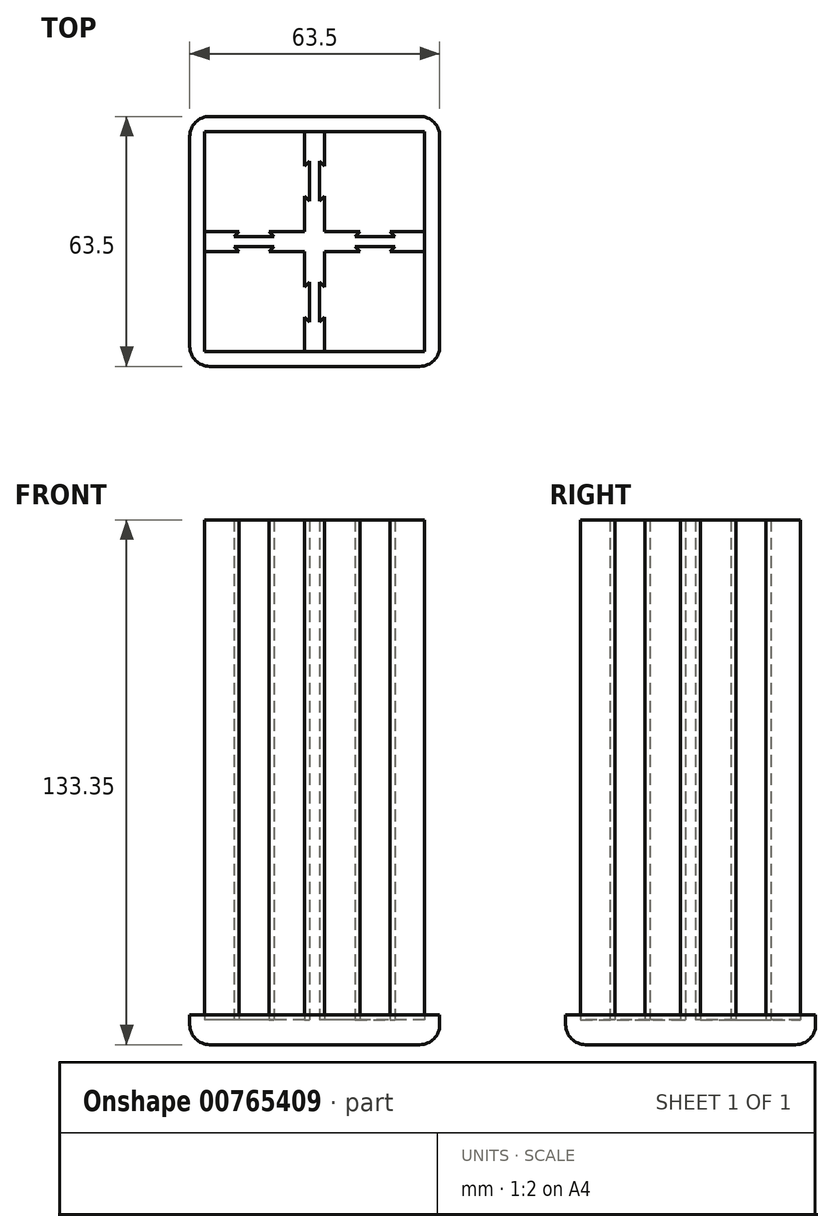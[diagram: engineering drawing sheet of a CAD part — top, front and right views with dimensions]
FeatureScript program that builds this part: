
annotation { "Feature Type Name" : "Feature", "Feature Type Description" : "" }
export const myFeature = defineFeature(function(context is Context, id is Id, definition is map)
    precondition{}
    {
        {
            var Q0;
            Q0=qCreatedBy(makeId("Top.planeOp"),FACE);
            var sketch = newSketch(context, id + "F0", { "sketchPlane" : qUnion([Q0])});
            skLineSegment(sketch, "E0.bottom", {"start": v(-2.54, 27.94) * mm, "end": v(2.54, 27.94) * mm});
            skLineSegment(sketch, "E0.top", {"start": v(-2.54, -27.94) * mm, "end": v(2.54, -27.94) * mm});
            skLineSegment(sketch, "E0.left", {"start": v(-2.54, 27.94) * mm, "end": v(-2.54, -27.94) * mm});
            skLineSegment(sketch, "E0.right", {"start": v(2.54, 27.94) * mm, "end": v(2.54, -27.94) * mm});
            skPoint(sketch, "E0.middle", {"position": v(0, 0) * mm});
            skLineSegment(sketch, "E1.bottom", {"start": v(27.94, 2.54) * mm, "end": v(-27.94, 2.54) * mm});
            skLineSegment(sketch, "E1.top", {"start": v(27.94, -2.54) * mm, "end": v(-27.94, -2.54) * mm});
            skLineSegment(sketch, "E1.left", {"start": v(27.94, 2.54) * mm, "end": v(27.94, -2.54) * mm});
            skLineSegment(sketch, "E1.right", {"start": v(-27.94, 2.54) * mm, "end": v(-27.94, -2.54) * mm});
            skLineSegment(sketch, "E2.bottom", {"start": v(2.54, 15.37) * mm, "end": v(1.27, 15.37) * mm});
            skLineSegment(sketch, "E2.top", {"start": v(2.54, -15.37) * mm, "end": v(1.27, -15.37) * mm});
            skLineSegment(sketch, "E2.left", {"start": v(15.37, 2.54) * mm, "end": v(15.37, 1.27) * mm});
            skLineSegment(sketch, "E2.right", {"start": v(-15.37, 2.54) * mm, "end": v(-15.37, 1.27) * mm});
            skLineSegment(sketch, "E3", {"start": v(-15.37, 2.54) * mm, "end": v(-11.56, 2.54) * mm});
            skLineSegment(sketch, "E4", {"start": v(-11.56, 2.54) * mm, "end": v(-10.29, 1.27) * mm});
            skLineSegment(sketch, "E5", {"start": v(-10.29, 1.27) * mm, "end": v(-15.37, 1.27) * mm});
            skLineSegment(sketch, "E6", {"start": v(-15.37, 1.27) * mm, "end": v(-15.37, 2.54) * mm});
            skLineSegment(sketch, "E7.MirrorCS", {"start": v(-20.45, 1.27) * mm, "end": v(-15.37, 1.27) * mm});
            skLineSegment(sketch, "E8.MirrorCS", {"start": v(-19.18, 2.54) * mm, "end": v(-20.45, 1.27) * mm});
            skLineSegment(sketch, "E9.MirrorCS", {"start": v(-15.37, 2.54) * mm, "end": v(-19.18, 2.54) * mm});
            skLineSegment(sketch, "E10.MirrorCS", {"start": v(-10.29, -1.27) * mm, "end": v(-15.37, -1.27) * mm});
            skLineSegment(sketch, "E11.MirrorCS", {"start": v(-20.45, -1.27) * mm, "end": v(-15.37, -1.27) * mm});
            skLineSegment(sketch, "E12.MirrorCS", {"start": v(-15.37, -2.54) * mm, "end": v(-19.18, -2.54) * mm});
            skLineSegment(sketch, "E13.MirrorCS", {"start": v(-19.18, -2.54) * mm, "end": v(-20.45, -1.27) * mm});
            skLineSegment(sketch, "E14.MirrorCS", {"start": v(-15.37, -2.54) * mm, "end": v(-11.56, -2.54) * mm});
            skLineSegment(sketch, "E15.MirrorCS", {"start": v(-11.56, -2.54) * mm, "end": v(-10.29, -1.27) * mm});
            skLineSegment(sketch, "E16.MirrorCS", {"start": v(10.29, 1.27) * mm, "end": v(15.37, 1.27) * mm});
            skLineSegment(sketch, "E17.MirrorCS", {"start": v(20.45, 1.27) * mm, "end": v(15.37, 1.27) * mm});
            skLineSegment(sketch, "E18.MirrorCS", {"start": v(15.37, 2.54) * mm, "end": v(19.18, 2.54) * mm});
            skLineSegment(sketch, "E19.MirrorCS", {"start": v(19.18, 2.54) * mm, "end": v(20.45, 1.27) * mm});
            skLineSegment(sketch, "E20.MirrorCS", {"start": v(11.56, 2.54) * mm, "end": v(10.29, 1.27) * mm});
            skLineSegment(sketch, "E21.MirrorCS", {"start": v(15.37, 2.54) * mm, "end": v(11.56, 2.54) * mm});
            skLineSegment(sketch, "E22.MirrorCS", {"start": v(10.29, -1.27) * mm, "end": v(15.37, -1.27) * mm});
            skLineSegment(sketch, "E23.MirrorCS", {"start": v(11.56, -2.54) * mm, "end": v(10.29, -1.27) * mm});
            skLineSegment(sketch, "E24.MirrorCS", {"start": v(15.37, -2.54) * mm, "end": v(11.56, -2.54) * mm});
            skLineSegment(sketch, "E25.MirrorCS", {"start": v(15.37, -2.54) * mm, "end": v(19.18, -2.54) * mm});
            skLineSegment(sketch, "E26.MirrorCS", {"start": v(19.18, -2.54) * mm, "end": v(20.45, -1.27) * mm});
            skLineSegment(sketch, "E27.MirrorCS", {"start": v(20.45, -1.27) * mm, "end": v(15.37, -1.27) * mm});
            skLineSegment(sketch, "E28", {"start": v(-2.54, -15.37) * mm, "end": v(-2.54, -11.56) * mm});
            skLineSegment(sketch, "E29", {"start": v(-2.54, -11.56) * mm, "end": v(-1.27, -10.29) * mm});
            skLineSegment(sketch, "E30", {"start": v(-1.27, -10.29) * mm, "end": v(-1.27, -15.37) * mm});
            skLineSegment(sketch, "E31.MirrorCS", {"start": v(-1.27, -20.45) * mm, "end": v(-1.27, -15.37) * mm});
            skLineSegment(sketch, "E32.MirrorCS", {"start": v(-2.54, -19.18) * mm, "end": v(-1.27, -20.45) * mm});
            skLineSegment(sketch, "E33.MirrorCS", {"start": v(-2.54, -15.37) * mm, "end": v(-2.54, -19.18) * mm});
            skLineSegment(sketch, "E34.MirrorCS", {"start": v(1.27, -10.29) * mm, "end": v(1.27, -15.37) * mm});
            skLineSegment(sketch, "E35.MirrorCS", {"start": v(2.54, -11.56) * mm, "end": v(1.27, -10.29) * mm});
            skLineSegment(sketch, "E36.MirrorCS", {"start": v(2.54, -15.37) * mm, "end": v(2.54, -11.56) * mm});
            skLineSegment(sketch, "E37.MirrorCS", {"start": v(1.27, -20.45) * mm, "end": v(1.27, -15.37) * mm});
            skLineSegment(sketch, "E38.MirrorCS", {"start": v(2.54, -19.18) * mm, "end": v(1.27, -20.45) * mm});
            skLineSegment(sketch, "E39.MirrorCS", {"start": v(-1.27, 10.29) * mm, "end": v(-1.27, 15.37) * mm});
            skLineSegment(sketch, "E40.MirrorCS", {"start": v(-1.27, 20.45) * mm, "end": v(-1.27, 15.37) * mm});
            skLineSegment(sketch, "E41.MirrorCS", {"start": v(-2.54, -27.94) * mm, "end": v(-2.54, 27.94) * mm});
            skLineSegment(sketch, "E42.MirrorCS", {"start": v(-2.54, 19.18) * mm, "end": v(-1.27, 20.45) * mm});
            skLineSegment(sketch, "E43.MirrorCS", {"start": v(-2.54, 11.56) * mm, "end": v(-1.27, 10.29) * mm});
            skLineSegment(sketch, "E44.MirrorCS", {"start": v(1.27, 10.29) * mm, "end": v(1.27, 15.37) * mm});
            skLineSegment(sketch, "E45.MirrorCS", {"start": v(1.27, 20.45) * mm, "end": v(1.27, 15.37) * mm});
            skLineSegment(sketch, "E46.MirrorCS", {"start": v(2.54, 19.18) * mm, "end": v(1.27, 20.45) * mm});
            skLineSegment(sketch, "E47.MirrorCS", {"start": v(2.54, 11.56) * mm, "end": v(1.27, 10.29) * mm});
            skPoint(sketch, "E48.orphan", {"position": v(-15.37, -15.37) * mm});
            skPoint(sketch, "E49.orphan", {"position": v(15.37, -15.37) * mm});
            skPoint(sketch, "E50.orphan", {"position": v(15.37, 15.37) * mm});
            skLineSegment(sketch, "E51.trimOffspring", {"start": v(-1.27, 15.37) * mm, "end": v(-2.54, 15.37) * mm});
            skLineSegment(sketch, "E52.trimOffspring", {"start": v(-1.27, -15.37) * mm, "end": v(-2.54, -15.37) * mm});
            skLineSegment(sketch, "E53.trimOffspring", {"start": v(15.37, -1.27) * mm, "end": v(15.37, -2.54) * mm});
            skLineSegment(sketch, "E54.trimOffspring", {"start": v(-15.37, -1.27) * mm, "end": v(-15.37, -2.54) * mm});
            skPoint(sketch, "E55.orphan", {"position": v(-15.37, 15.37) * mm});
            skSolve(sketch);
        }
        {
            var Q0;
            {var subQ7=sQuery(id+"F0.wireOp",EDGE,"E0.top");Q0=makeQuery(id+"F0.imprint","IMPRINT",FACE,{"disambiguationData":[TD([[makeQuery(id+"F0.imprint","IMPRINT",EDGE,{"derivedFrom":subQ7}),1.0]])]});}
            var Q1;
            {var subQ0=sQuery(id+"F0.wireOp",EDGE,"E0.right");var subQ1=sQuery(id+"F0.wireOp",EDGE,"E1.bottom");var subQ2=makeQuery(id+"F0.imprint","INTERSECT",VERTEX,{"derivedFrom":[subQ1,subQ0]});Q1=makeQuery(id+"F0.imprint","IMPRINT",FACE,{"disambiguationData":[TD([[makeQuery(id+"F0.imprint","IMPRINT",EDGE,{"disambiguationData":[TD([[subQ2,-1.0]])],"derivedFrom":subQ1}),1.0]])]});}
            var Q2;
            {var subQ6=sQuery(id+"F0.wireOp",EDGE,"E1.right");Q2=makeQuery(id+"F0.imprint","IMPRINT",FACE,{"disambiguationData":[TD([[makeQuery(id+"F0.imprint","IMPRINT",EDGE,{"derivedFrom":subQ6}),1.0]])]});}
            var Q3;
            {var subQ1=sQuery(id+"F0.wireOp",EDGE,"E0.bottom");Q3=makeQuery(id+"F0.imprint","IMPRINT",FACE,{"disambiguationData":[TD([[makeQuery(id+"F0.imprint","IMPRINT",EDGE,{"derivedFrom":subQ1}),-1.0]])]});}
            var Q4;
            {var subQ6=sQuery(id+"F0.wireOp",EDGE,"E1.left");Q4=makeQuery(id+"F0.imprint","IMPRINT",FACE,{"disambiguationData":[TD([[makeQuery(id+"F0.imprint","IMPRINT",EDGE,{"derivedFrom":subQ6}),-1.0]])]});}
            extrude(context, id + "F1", {"entities" : qUnion([Q0, Q1, Q2, Q3, Q4]), "depth" : 127 * mm, "offsetDistance" : 25.4 * mm});
        }
        {
            var Q0;
            Q0=makeQuery(id+"F1.opExtrude","CAP_FACE",FACE,{"disambiguationData":[OSD([sQuery(id+"F0.wireOp",EDGE,"E0.bottom"),sQuery(id+"F0.wireOp",EDGE,"E0.top"),sQuery(id+"F0.wireOp",EDGE,"E1.bottom"),sQuery(id+"F0.wireOp",EDGE,"E1.top"),sQuery(id+"F0.wireOp",EDGE,"E1.left"),sQuery(id+"F0.wireOp",EDGE,"E1.right"),sQuery(id+"F0.wireOp",EDGE,"E4"),sQuery(id+"F0.wireOp",EDGE,"E5"),sQuery(id+"F0.wireOp",EDGE,"E7.MirrorCS"),sQuery(id+"F0.wireOp",EDGE,"E8.MirrorCS"),sQuery(id+"F0.wireOp",EDGE,"E10.MirrorCS"),sQuery(id+"F0.wireOp",EDGE,"E11.MirrorCS"),sQuery(id+"F0.wireOp",EDGE,"E13.MirrorCS"),sQuery(id+"F0.wireOp",EDGE,"E15.MirrorCS"),sQuery(id+"F0.wireOp",EDGE,"E16.MirrorCS"),sQuery(id+"F0.wireOp",EDGE,"E17.MirrorCS"),sQuery(id+"F0.wireOp",EDGE,"E19.MirrorCS"),sQuery(id+"F0.wireOp",EDGE,"E20.MirrorCS"),sQuery(id+"F0.wireOp",EDGE,"E22.MirrorCS"),sQuery(id+"F0.wireOp",EDGE,"E23.MirrorCS"),sQuery(id+"F0.wireOp",EDGE,"E26.MirrorCS"),sQuery(id+"F0.wireOp",EDGE,"E27.MirrorCS"),sQuery(id+"F0.wireOp",EDGE,"E29"),sQuery(id+"F0.wireOp",EDGE,"E30"),sQuery(id+"F0.wireOp",EDGE,"E31.MirrorCS"),sQuery(id+"F0.wireOp",EDGE,"E32.MirrorCS"),sQuery(id+"F0.wireOp",EDGE,"E0.right"),sQuery(id+"F0.wireOp",EDGE,"E34.MirrorCS"),sQuery(id+"F0.wireOp",EDGE,"E35.MirrorCS"),sQuery(id+"F0.wireOp",EDGE,"E37.MirrorCS"),sQuery(id+"F0.wireOp",EDGE,"E38.MirrorCS"),sQuery(id+"F0.wireOp",EDGE,"E39.MirrorCS"),sQuery(id+"F0.wireOp",EDGE,"E40.MirrorCS"),sQuery(id+"F0.wireOp",EDGE,"E41.MirrorCS"),sQuery(id+"F0.wireOp",EDGE,"E42.MirrorCS"),sQuery(id+"F0.wireOp",EDGE,"E43.MirrorCS"),sQuery(id+"F0.wireOp",EDGE,"E44.MirrorCS"),sQuery(id+"F0.wireOp",EDGE,"E45.MirrorCS"),sQuery(id+"F0.wireOp",EDGE,"E46.MirrorCS"),sQuery(id+"F0.wireOp",EDGE,"E47.MirrorCS")])],"isStart":true});
            var sketch = newSketch(context, id + "F2", { "sketchPlane" : qUnion([Q0])});
            skLineSegment(sketch, "E56.bottom", {"start": v(27.94, 27.94) * mm, "end": v(-27.94, 27.94) * mm});
            skLineSegment(sketch, "E56.top", {"start": v(27.94, -27.94) * mm, "end": v(-27.94, -27.94) * mm});
            skLineSegment(sketch, "E56.left", {"start": v(27.94, 27.94) * mm, "end": v(27.94, -27.94) * mm});
            skLineSegment(sketch, "E56.right", {"start": v(-27.94, 27.94) * mm, "end": v(-27.94, -27.94) * mm});
            skPoint(sketch, "E56.middle", {"position": v(0, 0) * mm});
            skSolve(sketch);
        }
        {
            var Q0;
            Q0 = qSketchRegion(id + "F2", true);
            extrude(context, id + "F3", {"entities" : qUnion([Q0]), "operationType" : NewBodyOperationType.ADD, "depth" : 2.54 * mm, "offsetDistance" : 25.4 * mm});
        }
        {
            var Q0;
            Q0=makeQuery(id+"F3.opExtrude","CAP_FACE",FACE,{"disambiguationData":[OSD([sQuery(id+"F2.wireOp",EDGE,"E56.bottom"),sQuery(id+"F2.wireOp",EDGE,"E56.top"),sQuery(id+"F2.wireOp",EDGE,"E56.left"),sQuery(id+"F2.wireOp",EDGE,"E56.right")])],"isStart":false});
            var sketch = newSketch(context, id + "F4", { "sketchPlane" : qUnion([Q0])});
            skLineSegment(sketch, "E57.bottom", {"start": v(27.94, 27.94) * mm, "end": v(-27.94, 27.94) * mm});
            skLineSegment(sketch, "E57.top", {"start": v(27.94, -27.94) * mm, "end": v(-27.94, -27.94) * mm});
            skLineSegment(sketch, "E57.left", {"start": v(27.94, 27.94) * mm, "end": v(27.94, -27.94) * mm});
            skLineSegment(sketch, "E57.right", {"start": v(-27.94, 27.94) * mm, "end": v(-27.94, -27.94) * mm});
            skPoint(sketch, "E57.middle", {"position": v(0, 0) * mm});
            skLineSegment(sketch, "E58.0", {"start": v(31.75, 31.75) * mm, "end": v(-31.75, 31.75) * mm});
            skLineSegment(sketch, "E58.1", {"start": v(31.75, 31.75) * mm, "end": v(31.75, -31.75) * mm});
            skLineSegment(sketch, "E58.2", {"start": v(31.75, -31.75) * mm, "end": v(-31.75, -31.75) * mm});
            skLineSegment(sketch, "E58.3", {"start": v(-31.75, 31.75) * mm, "end": v(-31.75, -31.75) * mm});
            skSolve(sketch);
        }
        {
            var Q0;
            Q0=makeQuery(id+"F4.imprint","IMPRINT",FACE,{"disambiguationData":[TD([[makeQuery(id+"F4.imprint","IMPRINT",EDGE,{"derivedFrom":sQuery(id+"F4.wireOp",EDGE,"E57.bottom")}),-1.0]])]});
            var Q1;
            Q1=makeQuery(id+"F4.imprint","IMPRINT",FACE,{"disambiguationData":[TD([[makeQuery(id+"F4.imprint","IMPRINT",EDGE,{"derivedFrom":sQuery(id+"F4.wireOp",EDGE,"E57.bottom")}),1.0]])]});
            extrude(context, id + "F5", {"entities" : qUnion([Q0, Q1]), "depth" : 3.8 * mm, "offsetDistance" : 25.4 * mm});
        }
        {
            var Q0;
            Q0=makeQuery(id+"F4.imprint","IMPRINT",FACE,{"disambiguationData":[TD([[makeQuery(id+"F4.imprint","IMPRINT",EDGE,{"derivedFrom":sQuery(id+"F4.wireOp",EDGE,"E57.bottom")}),-1.0]])]});
            extrude(context, id + "F6", {"entities" : qUnion([Q0]), "operationType" : NewBodyOperationType.ADD, "oppositeDirection" : true, "depth" : 3.8 * mm, "offsetDistance" : 25.4 * mm});
        }
        {
            var Q0;
            {var subQ0=sQuery(id+"F4.wireOp",EDGE,"E58.3");var subQ1=sQuery(id+"F4.wireOp",EDGE,"E58.0");Q0=makeQuery(id+"F6.boolean.opBoolean","MERGE",EDGE,{"derivedFrom":[makeQuery(id+"F5.opExtrude","SWEPT_EDGE",EDGE,{"disambiguationData":[OSD([subQ1,subQ0])]}),makeQuery(id+"F6.opExtrude","SWEPT_EDGE",EDGE,{"disambiguationData":[OSD([subQ1,subQ0])]})]});}
            var Q1;
            {var subQ0=sQuery(id+"F4.wireOp",EDGE,"E58.1");var subQ1=sQuery(id+"F4.wireOp",EDGE,"E58.0");Q1=makeQuery(id+"F6.boolean.opBoolean","MERGE",EDGE,{"derivedFrom":[makeQuery(id+"F5.opExtrude","SWEPT_EDGE",EDGE,{"disambiguationData":[OSD([subQ1,subQ0])]}),makeQuery(id+"F6.opExtrude","SWEPT_EDGE",EDGE,{"disambiguationData":[OSD([subQ1,subQ0])]})]});}
            var Q2;
            {var subQ0=sQuery(id+"F4.wireOp",EDGE,"E58.2");var subQ1=sQuery(id+"F4.wireOp",EDGE,"E58.1");Q2=makeQuery(id+"F6.boolean.opBoolean","MERGE",EDGE,{"derivedFrom":[makeQuery(id+"F5.opExtrude","SWEPT_EDGE",EDGE,{"disambiguationData":[OSD([subQ1,subQ0])]}),makeQuery(id+"F6.opExtrude","SWEPT_EDGE",EDGE,{"disambiguationData":[OSD([subQ1,subQ0])]})]});}
            var Q3;
            Q3=makeQuery(id+"F5.opExtrude","CAP_EDGE",EDGE,{"disambiguationData":[OSD([sQuery(id+"F4.wireOp",EDGE,"E58.1")])],"isStart":false});
            var Q4;
            Q4=makeQuery(id+"F5.opExtrude","CAP_EDGE",EDGE,{"disambiguationData":[OSD([sQuery(id+"F4.wireOp",EDGE,"E58.0")])],"isStart":false});
            var Q5;
            {var subQ0=sQuery(id+"F4.wireOp",EDGE,"E58.3");var subQ1=sQuery(id+"F4.wireOp",EDGE,"E58.2");Q5=makeQuery(id+"F6.boolean.opBoolean","MERGE",EDGE,{"derivedFrom":[makeQuery(id+"F5.opExtrude","SWEPT_EDGE",EDGE,{"disambiguationData":[OSD([subQ1,subQ0])]}),makeQuery(id+"F6.opExtrude","SWEPT_EDGE",EDGE,{"disambiguationData":[OSD([subQ1,subQ0])]})]});}
            var Q6;
            Q6=makeQuery(id+"F5.opExtrude","CAP_EDGE",EDGE,{"disambiguationData":[OSD([sQuery(id+"F4.wireOp",EDGE,"E58.2")])],"isStart":false});
            var Q7;
            Q7=makeQuery(id+"F5.opExtrude","CAP_EDGE",EDGE,{"disambiguationData":[OSD([sQuery(id+"F4.wireOp",EDGE,"E58.3")])],"isStart":false});
            fillet(context, id + "F7", {"entities" : qUnion([Q0, Q1, Q2, Q3, Q4, Q5, Q6, Q7]), "radius" : 5.08 * mm, "tangentPropagation" : true, "allowEdgeOverflow" : false});
        }
    });
